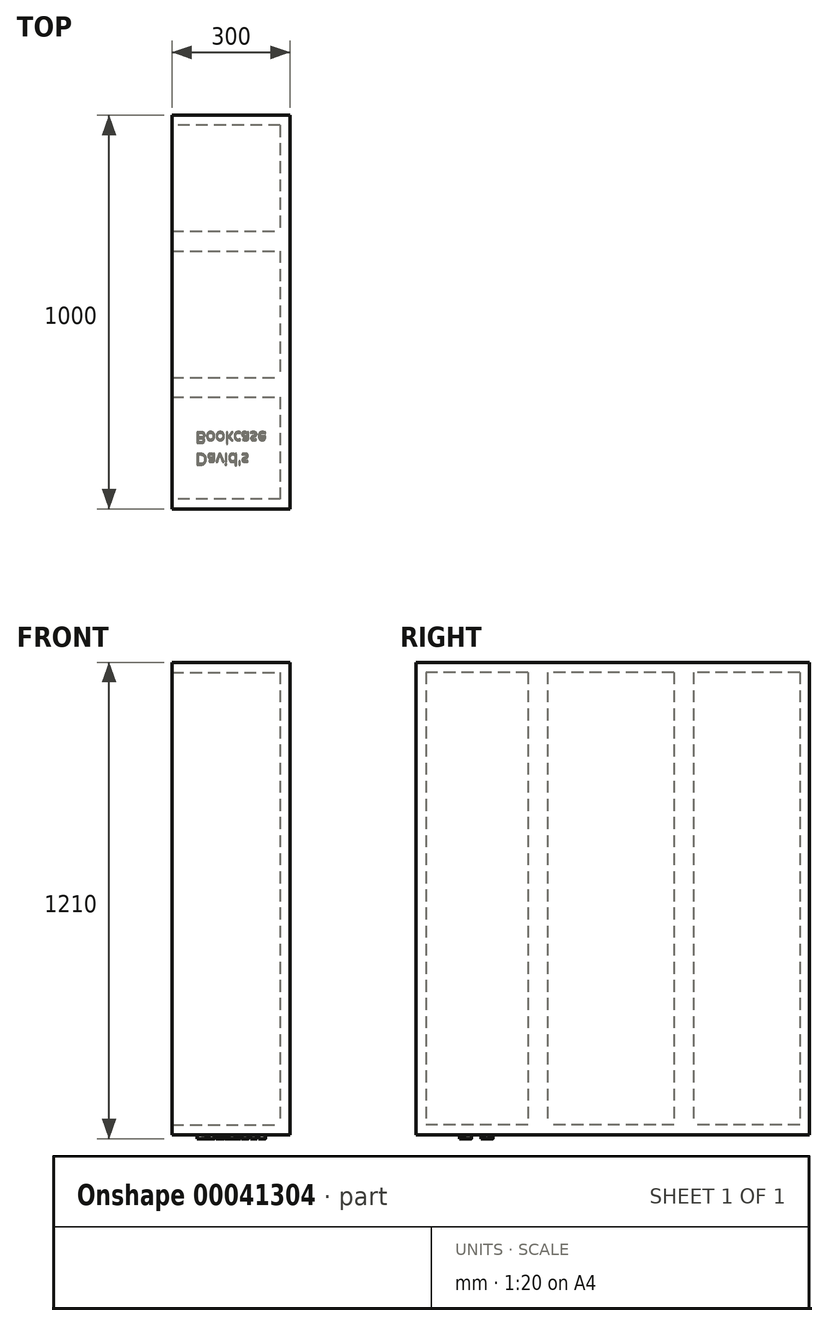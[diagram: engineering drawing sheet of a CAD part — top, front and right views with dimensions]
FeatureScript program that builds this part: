
annotation { "Feature Type Name" : "Feature", "Feature Type Description" : "" }
export const myFeature = defineFeature(function(context is Context, id is Id, definition is map)
    precondition{}
    {
        {
            var Q0;
            Q0=qCreatedBy(makeId("Top.planeOp"),FACE);
            var sketch = newSketch(context, id + "F0", { "sketchPlane" : qUnion([Q0])});
            skLineSegment(sketch, "E0.rect.bottom", {"start": v(150, 500) * mm, "end": v(-150, 500) * mm});
            skLineSegment(sketch, "E0.rect.top", {"start": v(150, -500) * mm, "end": v(-150, -500) * mm});
            skLineSegment(sketch, "E0.rect.left", {"start": v(150, 500) * mm, "end": v(150, -500) * mm});
            skLineSegment(sketch, "E0.rect.right", {"start": v(-150, 500) * mm, "end": v(-150, -500) * mm});
            skPoint(sketch, "E0.rect.middle", {"position": v(0, 0) * mm});
            skSolve(sketch);
        }
        {
            var Q0;
            Q0 = qSketchRegion(id + "F0", true);
            var Q1;
            Q1 = qSketchRegion(id + "F7PKYAq9P794cAb_1", true);
            extrude(context, id + "F1", {"entities" : qUnion([Q0, Q1]), "depth" : 1200 * mm});
        }
        {
            var Q0;
            Q0=makeQuery(id+"F1.opExtrude","SWEPT_FACE",FACE,{"disambiguationData":[OSD([sQuery(id+"F0.wireOp",EDGE,"E0.rect.right")])]});
            shell(context, id + "F2", {"entities" : qUnion([Q0]), "thickness" : 25 * mm});
        }
        {
            var Q0;
            Q0=makeQuery(id+"F2.opShell","OFFSET_FACE",FACE,{"disambiguationData":[OSD([sQuery(id+"F0.wireOp",EDGE,"E0.rect.left")])]});
            var sketch = newSketch(context, id + "F3", { "sketchPlane" : qUnion([Q0])});
            skLineSegment(sketch, "E1.bottom", {"start": v(215.85, 1175) * mm, "end": v(165.85, 1175) * mm});
            skLineSegment(sketch, "E1.top", {"start": v(215.85, 25) * mm, "end": v(165.85, 25) * mm});
            skLineSegment(sketch, "E1.left", {"start": v(215.85, 1175) * mm, "end": v(215.85, 25) * mm});
            skLineSegment(sketch, "E1.right", {"start": v(165.85, 1175) * mm, "end": v(165.85, 25) * mm});
            skLineSegment(sketch, "E2.left", {"start": v(-155.22, 1175) * mm, "end": v(-155.22, 25) * mm});
            skLineSegment(sketch, "E2.right", {"start": v(-205.22, 1175) * mm, "end": v(-205.22, 25) * mm});
            skLineSegment(sketch, "E2.bottom", {"start": v(-155.22, 1175) * mm, "end": v(-205.22, 1175) * mm});
            skLineSegment(sketch, "E2.top", {"start": v(-155.22, 25) * mm, "end": v(-205.22, 25) * mm});
            skSolve(sketch);
        }
        {
            var Q0;
            Q0 = qSketchRegion(id + "F3", true);
            extrude(context, id + "F4", {"entities" : qUnion([Q0]), "operationType" : NewBodyOperationType.ADD, "depth" : 275 * mm});
        }
        {
            var Q0;
            Q0=makeQuery(id+"F1.opExtrude","CAP_FACE",FACE,{"disambiguationData":[OSD([sQuery(id+"F0.wireOp",EDGE,"E0.rect.bottom"),sQuery(id+"F0.wireOp",EDGE,"E0.rect.top"),sQuery(id+"F0.wireOp",EDGE,"E0.rect.left"),sQuery(id+"F0.wireOp",EDGE,"E0.rect.right")])],"isStart":true});
            var sketch = newSketch(context, id + "F5", { "sketchPlane" : qUnion([Q0])});
            skText(sketch, "E3", { "text": "David\'s\nBookcase\n", "fontName": "OpenSans-Regular.ttf"});
            const initialGuessF5  = {"E3": [-0.0902, 0.35934, 1, 0, 0.02917]};
            skSetInitialGuess(sketch, initialGuessF5);
            skSolve(sketch);
        }
        {
            var Q0;
            Q0 = qSketchRegion(id + "F5", true);
            extrude(context, id + "F6", {"entities" : qUnion([Q0]), "operationType" : NewBodyOperationType.ADD, "depth" : 10 * mm});
        }
    });
